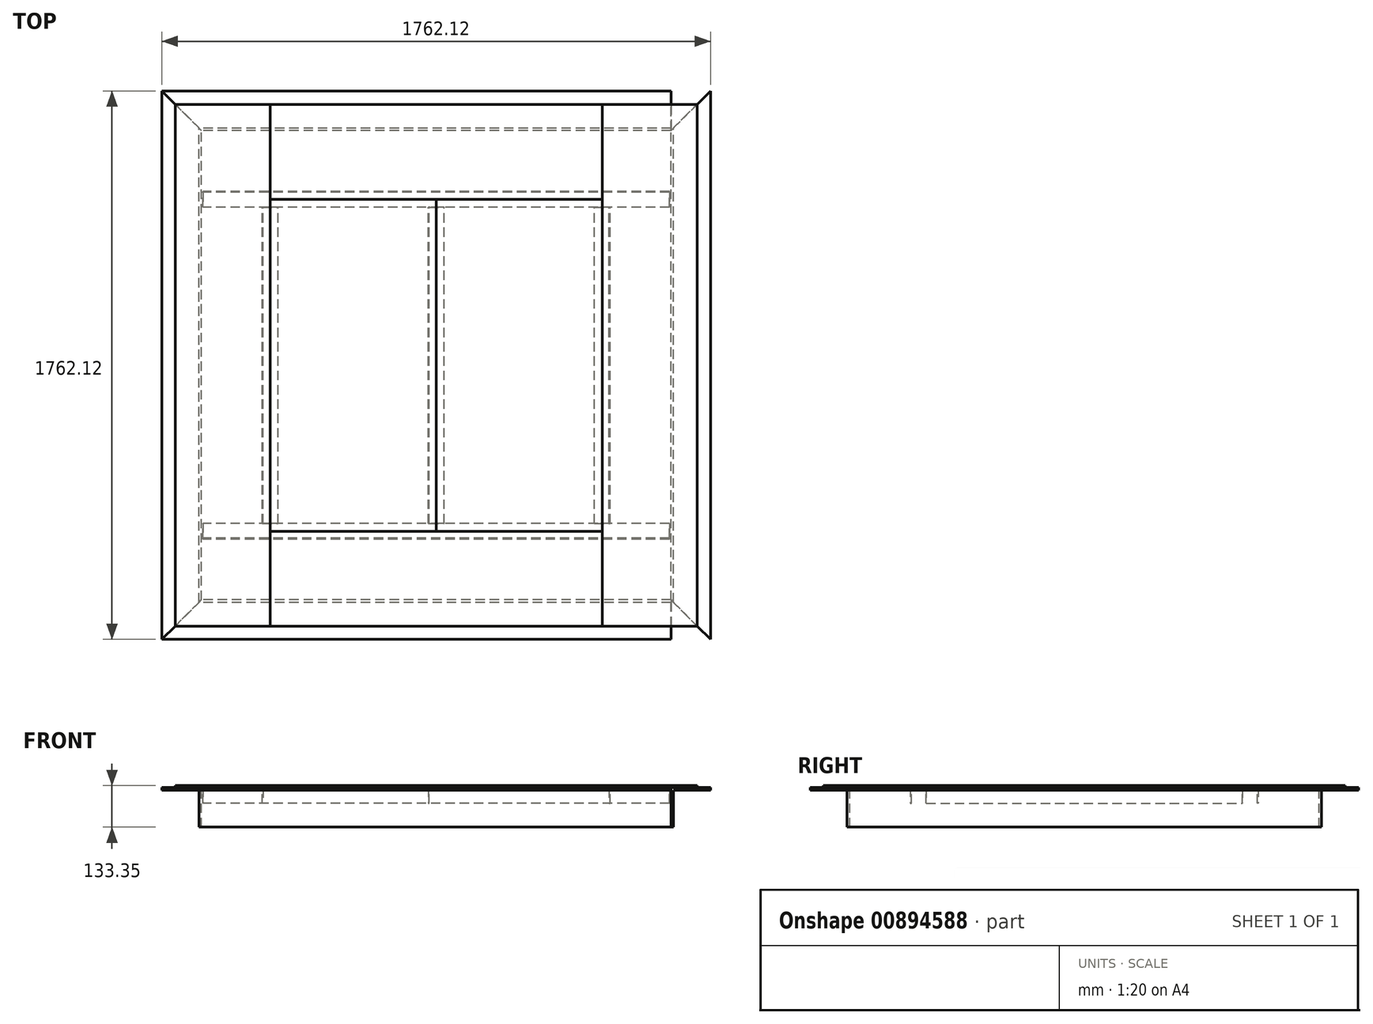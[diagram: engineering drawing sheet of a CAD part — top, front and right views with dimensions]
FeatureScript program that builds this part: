
annotation { "Feature Type Name" : "Feature", "Feature Type Description" : "" }
export const myFeature = defineFeature(function(context is Context, id is Id, definition is map)
    precondition{}
    {
        {
            var Q0;
            Q0=qCreatedBy(makeId("Right.planeOp"),FACE);
            var sketch = newSketch(context, id + "F0", { "sketchPlane" : qUnion([Q0])});
            skLineSegment(sketch, "E0", {"start": v(-754.06, 0) * mm, "end": v(-754.06, -127) * mm});
            skLineSegment(sketch, "E1", {"start": v(-754.06, 0) * mm, "end": v(-881.06, 0) * mm});
            skLineSegment(sketch, "E2", {"start": v(-881.06, 0) * mm, "end": v(-881.06, -7.94) * mm});
            skLineSegment(sketch, "E3", {"start": v(-754.06, -127) * mm, "end": v(-762, -127) * mm});
            skLineSegment(sketch, "E4", {"start": v(-762, -127) * mm, "end": v(-762, -7.94) * mm});
            skLineSegment(sketch, "E5", {"start": v(-762, -7.94) * mm, "end": v(-881.06, -7.94) * mm});
            skSolve(sketch);
        }
        {
            var Q0;
            Q0 = qSketchRegion(id + "F0", true);
            extrude(context, id + "F1", {"entities" : qUnion([Q0]), "endBound" : BoundingType.SYMMETRIC, "depth" : 1762.12 * mm, "offsetDistance" : 25.4 * mm});
        }
        {
            var Q0;
            Q0=makeQuery(id+"F1.opExtrude","SWEPT_FACE",FACE,{"disambiguationData":[OSD([sQuery(id+"F0.wireOp",EDGE,"E1")])]});
            var sketch = newSketch(context, id + "F2", { "sketchPlane" : qUnion([Q0])});
            skLineSegment(sketch, "E6.0", {"start": v(-881.06, -754.06) * mm, "end": v(-881.06, -881.06) * mm});
            skLineSegment(sketch, "E7.0", {"start": v(881.06, -754.06) * mm, "end": v(-881.06, -754.06) * mm});
            skLineSegment(sketch, "E8", {"start": v(-881.06, -754.06) * mm, "end": v(-754.06, -754.06) * mm});
            skLineSegment(sketch, "E9", {"start": v(-754.06, -754.06) * mm, "end": v(-881.06, -881.06) * mm});
            skLineSegment(sketch, "E10.0", {"start": v(881.06, -754.06) * mm, "end": v(881.06, -881.06) * mm});
            skLineSegment(sketch, "E11", {"start": v(881.06, -754.06) * mm, "end": v(754.06, -754.06) * mm});
            skLineSegment(sketch, "E12", {"start": v(754.06, -754.06) * mm, "end": v(881.06, -881.06) * mm});
            skSolve(sketch);
        }
        {
            var Q0;
            Q0 = qSketchRegion(id + "F2", true);
            extrude(context, id + "F3", {"entities" : qUnion([Q0]), "operationType" : NewBodyOperationType.REMOVE, "oppositeDirection" : true, "depth" : 152.4 * mm, "offsetDistance" : 25.4 * mm});
        }
        {
            var Q0;
            Q0=makeQuery(id+"F1.opExtrude","SWEPT_BODY",BODY,{"disambiguationData":[OSD([sQuery(id+"F0.wireOp",EDGE,"E0"),sQuery(id+"F0.wireOp",EDGE,"E1"),sQuery(id+"F0.wireOp",EDGE,"E2"),sQuery(id+"F0.wireOp",EDGE,"E3"),sQuery(id+"F0.wireOp",EDGE,"E4"),sQuery(id+"F0.wireOp",EDGE,"E5")])]});
            var Q1;
            Q1=qCreatedBy(makeId("Front.planeOp"),FACE);
            mirror(context, id + "F4", {"entities" : qUnion([Q0]), "mirrorPlane" : qUnion([Q1])});
        }
        {
            var Q0;
            Q0=qCreatedBy(makeId("Front.planeOp"),FACE);
            var sketch = newSketch(context, id + "F5", { "sketchPlane" : qUnion([Q0])});
            skLineSegment(sketch, "E13", {"start": v(754.06, 0) * mm, "end": v(754.06, -127) * mm});
            skLineSegment(sketch, "E14", {"start": v(754.06, -127) * mm, "end": v(762, -127) * mm});
            skLineSegment(sketch, "E15", {"start": v(754.06, 0) * mm, "end": v(881.06, 0) * mm});
            skLineSegment(sketch, "E16", {"start": v(881.06, 0) * mm, "end": v(881.06, -7.94) * mm});
            skLineSegment(sketch, "E17", {"start": v(881.06, -7.94) * mm, "end": v(762, -7.94) * mm});
            skLineSegment(sketch, "E18", {"start": v(762, -7.94) * mm, "end": v(762, -127) * mm});
            skSolve(sketch);
        }
        {
            var Q0;
            Q0 = qSketchRegion(id + "F5", true);
            extrude(context, id + "F6", {"entities" : qUnion([Q0]), "endBound" : BoundingType.SYMMETRIC, "depth" : 1762.12 * mm, "offsetDistance" : 25.4 * mm});
        }
        {
            var Q0;
            Q0=makeQuery(id+"F6.opExtrude","SWEPT_FACE",FACE,{"disambiguationData":[OSD([sQuery(id+"F5.wireOp",EDGE,"E15")])]});
            var sketch = newSketch(context, id + "F7", { "sketchPlane" : qUnion([Q0])});
            skLineSegment(sketch, "E19.0", {"start": v(754.06, 881.06) * mm, "end": v(881.06, 881.06) * mm});
            skLineSegment(sketch, "E20", {"start": v(754.06, 881.06) * mm, "end": v(754.06, 754.06) * mm});
            skLineSegment(sketch, "E21", {"start": v(754.06, 754.06) * mm, "end": v(881.06, 881.06) * mm});
            skLineSegment(sketch, "E22.0", {"start": v(754.06, -881.06) * mm, "end": v(881.06, -881.06) * mm});
            skLineSegment(sketch, "E23", {"start": v(754.06, -881.06) * mm, "end": v(754.06, -754.06) * mm});
            skLineSegment(sketch, "E24", {"start": v(754.06, -754.06) * mm, "end": v(881.06, -881.06) * mm});
            skSolve(sketch);
        }
        {
            var Q0;
            Q0 = qSketchRegion(id + "F7", true);
            extrude(context, id + "F8", {"entities" : qUnion([Q0]), "operationType" : NewBodyOperationType.REMOVE, "oppositeDirection" : true, "depth" : 152.4 * mm, "offsetDistance" : 25.4 * mm});
        }
        {
            var Q0;
            Q0=makeQuery(id+"F6.opExtrude","SWEPT_BODY",BODY,{"disambiguationData":[OSD([sQuery(id+"F5.wireOp",EDGE,"E13"),sQuery(id+"F5.wireOp",EDGE,"E14"),sQuery(id+"F5.wireOp",EDGE,"E15"),sQuery(id+"F5.wireOp",EDGE,"E16"),sQuery(id+"F5.wireOp",EDGE,"E17"),sQuery(id+"F5.wireOp",EDGE,"E18")])]});
            var Q1;
            Q1=qCreatedBy(makeId("Right.planeOp"),FACE);
            mirror(context, id + "F9", {"entities" : qUnion([Q0]), "mirrorPlane" : qUnion([Q1])});
        }
        {
            var Q0;
            Q0=qCreatedBy(makeId("Top.planeOp"),FACE);
            var sketch = newSketch(context, id + "F10", { "sketchPlane" : qUnion([Q0])});
            skLineSegment(sketch, "E25.0", {"start": v(-881.06, -881.06) * mm, "end": v(-881.06, 881.06) * mm});
            skLineSegment(sketch, "E26.0", {"start": v(881.06, -881.06) * mm, "end": v(881.06, 881.06) * mm});
            skLineSegment(sketch, "E27.bottom", {"start": v(-838.2, 838.2) * mm, "end": v(-533.4, 838.2) * mm});
            skLineSegment(sketch, "E27.top", {"start": v(-838.2, -838.2) * mm, "end": v(-533.4, -838.2) * mm});
            skLineSegment(sketch, "E27.left", {"start": v(-838.2, 838.2) * mm, "end": v(-838.2, -838.2) * mm});
            skLineSegment(sketch, "E27.right", {"start": v(-533.4, 838.2) * mm, "end": v(-533.4, -838.2) * mm});
            skSolve(sketch);
        }
        {
            var Q0;
            Q0 = qSketchRegion(id + "F10", true);
            extrude(context, id + "F11", {"entities" : qUnion([Q0]), "depth" : 6.35 * mm, "offsetDistance" : 25.4 * mm});
        }
        {
            var Q0;
            Q0=makeQuery(id+"F11.opExtrude","SWEPT_BODY",BODY,{"disambiguationData":[OSD([sQuery(id+"F10.wireOp",EDGE,"E27.bottom"),sQuery(id+"F10.wireOp",EDGE,"E27.top"),sQuery(id+"F10.wireOp",EDGE,"E27.left"),sQuery(id+"F10.wireOp",EDGE,"E27.right")])]});
            var Q1;
            Q1=qCreatedBy(makeId("Right.planeOp"),FACE);
            mirror(context, id + "F12", {"entities" : qUnion([Q0]), "mirrorPlane" : qUnion([Q1])});
        }
        {
            var Q0;
            Q0=qCreatedBy(makeId("Top.planeOp"),FACE);
            var sketch = newSketch(context, id + "F13", { "sketchPlane" : qUnion([Q0])});
            skLineSegment(sketch, "E28.bottom", {"start": v(-533.4, 838.2) * mm, "end": v(533.4, 838.2) * mm});
            skLineSegment(sketch, "E28.top", {"start": v(-533.4, 533.4) * mm, "end": v(533.4, 533.4) * mm});
            skLineSegment(sketch, "E28.left", {"start": v(-533.4, 838.2) * mm, "end": v(-533.4, 533.4) * mm});
            skLineSegment(sketch, "E28.right", {"start": v(533.4, 838.2) * mm, "end": v(533.4, 533.4) * mm});
            skSolve(sketch);
        }
        {
            var Q0;
            Q0 = qSketchRegion(id + "F13", true);
            extrude(context, id + "F14", {"entities" : qUnion([Q0]), "depth" : 6.35 * mm, "offsetDistance" : 25.4 * mm});
        }
        {
            var Q0;
            Q0=makeQuery(id+"F14.opExtrude","SWEPT_BODY",BODY,{"disambiguationData":[OSD([sQuery(id+"F13.wireOp",EDGE,"E28.bottom"),sQuery(id+"F13.wireOp",EDGE,"E28.top"),sQuery(id+"F13.wireOp",EDGE,"E28.left"),sQuery(id+"F13.wireOp",EDGE,"E28.right")])]});
            var Q1;
            Q1=qCreatedBy(makeId("Front.planeOp"),FACE);
            mirror(context, id + "F15", {"entities" : qUnion([Q0]), "mirrorPlane" : qUnion([Q1])});
        }
        {
            var Q0;
            Q0=qCreatedBy(makeId("Top.planeOp"),FACE);
            var sketch = newSketch(context, id + "F16", { "sketchPlane" : qUnion([Q0])});
            skLineSegment(sketch, "E29.bottom", {"start": v(-533.4, 533.4) * mm, "end": v(0, 533.4) * mm});
            skLineSegment(sketch, "E29.top", {"start": v(-533.4, -533.4) * mm, "end": v(0, -533.4) * mm});
            skLineSegment(sketch, "E29.left", {"start": v(-533.4, 533.4) * mm, "end": v(-533.4, -533.4) * mm});
            skLineSegment(sketch, "E29.right", {"start": v(0, 533.4) * mm, "end": v(0, -533.4) * mm});
            skSolve(sketch);
        }
        {
            var Q0;
            Q0 = qSketchRegion(id + "F16", true);
            extrude(context, id + "F17", {"entities" : qUnion([Q0]), "depth" : 6.35 * mm, "offsetDistance" : 25.4 * mm});
        }
        {
            var Q0;
            Q0=makeQuery(id+"F17.opExtrude","SWEPT_BODY",BODY,{"disambiguationData":[OSD([sQuery(id+"F16.wireOp",EDGE,"E29.bottom"),sQuery(id+"F16.wireOp",EDGE,"E29.top"),sQuery(id+"F16.wireOp",EDGE,"E29.left"),sQuery(id+"F16.wireOp",EDGE,"E29.right")])]});
            var Q1;
            Q1=qCreatedBy(makeId("Right.planeOp"),FACE);
            mirror(context, id + "F18", {"entities" : qUnion([Q0]), "mirrorPlane" : qUnion([Q1])});
        }
        {
            var Q0;
            Q0=qCreatedBy(makeId("Right.planeOp"),FACE);
            var sketch = newSketch(context, id + "F19", { "sketchPlane" : qUnion([Q0])});
            skLineSegment(sketch, "E30", {"start": v(-558.8, 0) * mm, "end": v(-558.8, -50.8) * mm});
            skLineSegment(sketch, "E31", {"start": v(-558.8, -50.8) * mm, "end": v(-555.62, -50.8) * mm});
            skLineSegment(sketch, "E32", {"start": v(-555.62, -50.8) * mm, "end": v(-555.62, -3.17) * mm});
            skLineSegment(sketch, "E33", {"start": v(-555.62, -3.17) * mm, "end": v(-508, -3.17) * mm});
            skLineSegment(sketch, "E34", {"start": v(-508, -3.17) * mm, "end": v(-508, 0) * mm});
            skLineSegment(sketch, "E35", {"start": v(-508, 0) * mm, "end": v(-558.8, 0) * mm});
            skSolve(sketch);
        }
        {
            var Q0;
            Q0 = qSketchRegion(id + "F19", true);
            extrude(context, id + "F20", {"entities" : qUnion([Q0]), "endBound" : BoundingType.SYMMETRIC, "depth" : 1498.6 * mm, "offsetDistance" : 25.4 * mm});
        }
        {
            var Q0;
            Q0=makeQuery(id+"F20.opExtrude","SWEPT_BODY",BODY,{"disambiguationData":[OSD([sQuery(id+"F19.wireOp",EDGE,"E30"),sQuery(id+"F19.wireOp",EDGE,"E31"),sQuery(id+"F19.wireOp",EDGE,"E32"),sQuery(id+"F19.wireOp",EDGE,"E33"),sQuery(id+"F19.wireOp",EDGE,"E34"),sQuery(id+"F19.wireOp",EDGE,"E35")])]});
            var Q1;
            Q1=qCreatedBy(makeId("Front.planeOp"),FACE);
            mirror(context, id + "F21", {"entities" : qUnion([Q0]), "mirrorPlane" : qUnion([Q1])});
        }
        {
            var Q0;
            Q0=qCreatedBy(makeId("Front.planeOp"),FACE);
            var sketch = newSketch(context, id + "F22", { "sketchPlane" : qUnion([Q0])});
            skLineSegment(sketch, "E36", {"start": v(-558.8, 0) * mm, "end": v(-508, 0) * mm});
            skLineSegment(sketch, "E37", {"start": v(-508, 0) * mm, "end": v(-508, -3.18) * mm});
            skLineSegment(sketch, "E38", {"start": v(-508, -3.18) * mm, "end": v(-555.62, -3.18) * mm});
            skLineSegment(sketch, "E39", {"start": v(-555.62, -3.18) * mm, "end": v(-555.62, -50.8) * mm});
            skLineSegment(sketch, "E40", {"start": v(-555.62, -50.8) * mm, "end": v(-558.8, -50.8) * mm});
            skLineSegment(sketch, "E41", {"start": v(-558.8, -50.8) * mm, "end": v(-558.8, 0) * mm});
            skSolve(sketch);
        }
        {
            var Q0;
            Q0 = qSketchRegion(id + "F22", true);
            extrude(context, id + "F23", {"entities" : qUnion([Q0]), "endBound" : BoundingType.SYMMETRIC, "depth" : 1016 * mm, "offsetDistance" : 25.4 * mm});
        }
        {
            var Q0;
            Q0=makeQuery(id+"F23.opExtrude","SWEPT_BODY",BODY,{"disambiguationData":[OSD([sQuery(id+"F22.wireOp",EDGE,"E36"),sQuery(id+"F22.wireOp",EDGE,"E37"),sQuery(id+"F22.wireOp",EDGE,"E38"),sQuery(id+"F22.wireOp",EDGE,"E39"),sQuery(id+"F22.wireOp",EDGE,"E40"),sQuery(id+"F22.wireOp",EDGE,"E41")])]});
            var Q1;
            Q1=qCreatedBy(makeId("Right.planeOp"),FACE);
            mirror(context, id + "F24", {"entities" : qUnion([Q0]), "mirrorPlane" : qUnion([Q1])});
        }
        {
            var Q0;
            Q0=qCreatedBy(makeId("Front.planeOp"),FACE);
            var sketch = newSketch(context, id + "F25", { "sketchPlane" : qUnion([Q0])});
            skLineSegment(sketch, "E42", {"start": v(-25.4, 0) * mm, "end": v(-25.4, -50.8) * mm});
            skLineSegment(sketch, "E43", {"start": v(-25.4, -50.8) * mm, "end": v(-22.22, -50.8) * mm});
            skLineSegment(sketch, "E44", {"start": v(-22.22, -50.8) * mm, "end": v(-22.23, -3.17) * mm});
            skLineSegment(sketch, "E45", {"start": v(-22.23, -3.17) * mm, "end": v(25.4, -3.17) * mm});
            skLineSegment(sketch, "E46", {"start": v(25.4, -3.17) * mm, "end": v(25.4, 0) * mm});
            skLineSegment(sketch, "E47", {"start": v(25.4, 0) * mm, "end": v(-25.4, 0) * mm});
            skSolve(sketch);
        }
        {
            var Q0;
            Q0 = qSketchRegion(id + "F25", true);
            extrude(context, id + "F26", {"entities" : qUnion([Q0]), "endBound" : BoundingType.SYMMETRIC, "depth" : 1016 * mm, "offsetDistance" : 25.4 * mm});
        }
    });
